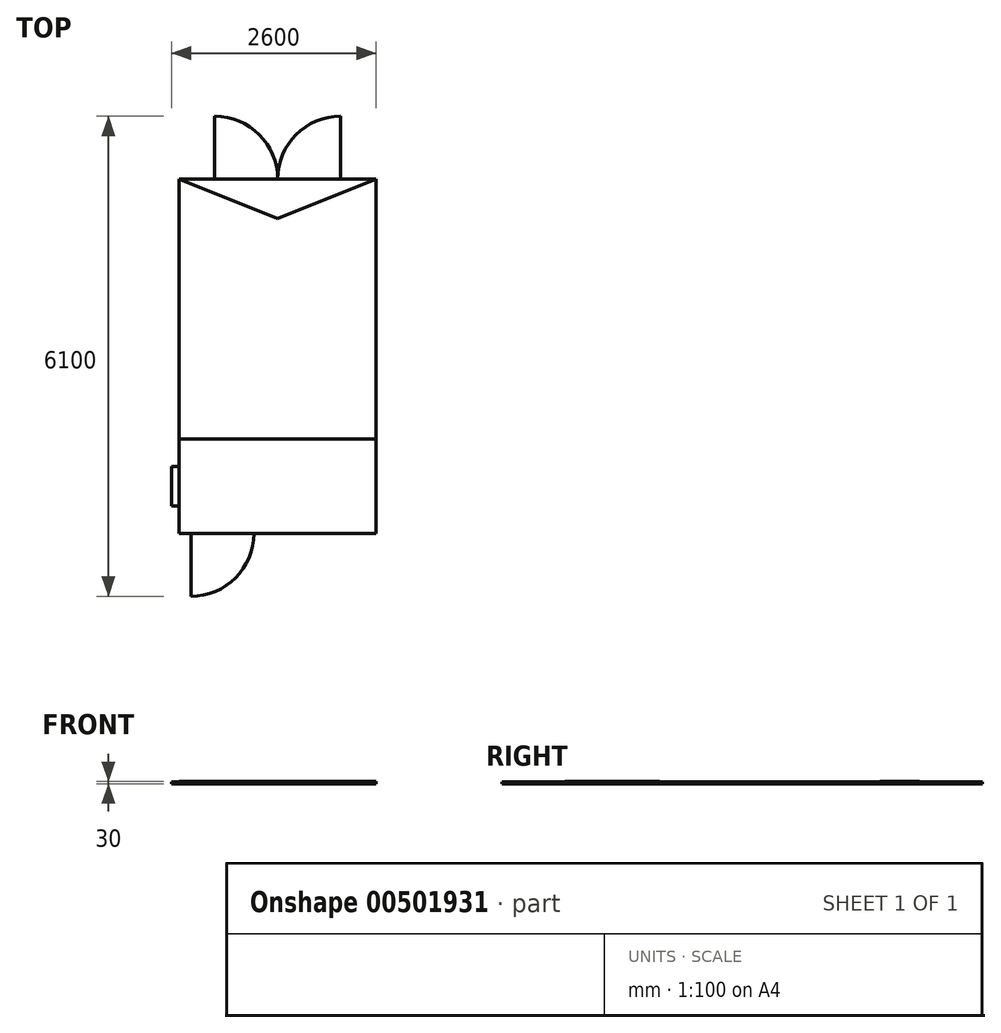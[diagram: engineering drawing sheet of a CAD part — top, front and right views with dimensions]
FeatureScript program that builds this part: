
annotation { "Feature Type Name" : "Feature", "Feature Type Description" : "" }
export const myFeature = defineFeature(function(context is Context, id is Id, definition is map)
    precondition{}
    {
        {
            var Q0;
            Q0=qCreatedBy(makeId("Top.planeOp"),FACE);
            var sketch = newSketch(context, id + "F0", { "sketchPlane" : qUnion([Q0])});
            skLineSegment(sketch, "E0.bottom", {"start": v(0, 0) * mm, "end": v(2500, 0) * mm});
            skLineSegment(sketch, "E0.top", {"start": v(0, 4500) * mm, "end": v(2500, 4500) * mm});
            skLineSegment(sketch, "E0.left", {"start": v(0, 0) * mm, "end": v(0, 4500) * mm});
            skLineSegment(sketch, "E0.right", {"start": v(2500, 0) * mm, "end": v(2500, 4500) * mm});
            skLineSegment(sketch, "E1", {"start": v(0, 1200) * mm, "end": v(2500, 1200) * mm});
            skLineSegment(sketch, "E2", {"start": v(0, 4500) * mm, "end": v(1250, 4000) * mm});
            skLineSegment(sketch, "E3", {"start": v(1250, 4000) * mm, "end": v(2500, 4500) * mm});
            skLineSegment(sketch, "E4", {"start": v(450, 4500) * mm, "end": v(450, 5300) * mm});
            skArc(sketch, "E5", {"start": v(1250, 4500) * mm, "mid": v(1015.69, 5065.69) * mm, "end": v(450, 5300) * mm});
            skLineSegment(sketch, "E6", {"start": v(2050, 4500) * mm, "end": v(2050, 5300) * mm});
            skArc(sketch, "E7", {"start": v(2050, 5300) * mm, "mid": v(1484.31, 5065.69) * mm, "end": v(1250, 4500) * mm});
            skLineSegment(sketch, "E8", {"start": v(0, 850) * mm, "end": v(-100, 850) * mm});
            skLineSegment(sketch, "E9", {"start": v(-100, 850) * mm, "end": v(-100, 350) * mm});
            skLineSegment(sketch, "E10", {"start": v(-100, 350) * mm, "end": v(0, 350) * mm});
            skLineSegment(sketch, "E11", {"start": v(147.95, 0) * mm, "end": v(147.95, -800) * mm});
            skArc(sketch, "E12", {"start": v(147.95, -800) * mm, "mid": v(713.64, -565.69) * mm, "end": v(947.95, 0) * mm});
            skSolve(sketch);
        }
        {
            var Q0;
            {var subQ0=sQuery(id+"F0.wireOp",EDGE,"E4");Q0=makeQuery(id+"F0.imprint","IMPRINT",FACE,{"disambiguationData":[TD([[makeQuery(id+"F0.imprint","IMPRINT",EDGE,{"derivedFrom":subQ0}),-1.0]])]});}
            var Q1;
            {var subQ2=sQuery(id+"F0.wireOp",EDGE,"E6");Q1=makeQuery(id+"F0.imprint","IMPRINT",FACE,{"disambiguationData":[TD([[makeQuery(id+"F0.imprint","IMPRINT",EDGE,{"derivedFrom":subQ2}),1.0]])]});}
            var Q2;
            {var subQ1=sQuery(id+"F0.wireOp",EDGE,"E1");Q2=makeQuery(id+"F0.imprint","IMPRINT",FACE,{"disambiguationData":[TD([[makeQuery(id+"F0.imprint","IMPRINT",EDGE,{"derivedFrom":subQ1}),1.0]])]});}
            var Q3;
            {var subQ0=sQuery(id+"F0.wireOp",EDGE,"E8");Q3=makeQuery(id+"F0.imprint","IMPRINT",FACE,{"disambiguationData":[TD([[makeQuery(id+"F0.imprint","IMPRINT",EDGE,{"derivedFrom":subQ0}),1.0]])]});}
            var Q4;
            {var subQ0=sQuery(id+"F0.wireOp",EDGE,"E11");Q4=makeQuery(id+"F0.imprint","IMPRINT",FACE,{"disambiguationData":[TD([[makeQuery(id+"F0.imprint","IMPRINT",EDGE,{"derivedFrom":subQ0}),1.0]])]});}
            extrude(context, id + "F1", {"entities" : qUnion([Q0, Q1, Q2, Q3, Q4]), "depth" : 25 * mm});
        }
        {
            var Q0;
            {var subQ5=sQuery(id+"F0.wireOp",EDGE,"E2");Q0=makeQuery(id+"F0.imprint","IMPRINT",FACE,{"disambiguationData":[TD([[makeQuery(id+"F0.imprint","IMPRINT",EDGE,{"derivedFrom":subQ5}),1.0]])]});}
            extrude(context, id + "F2", {"entities" : qUnion([Q0]), "operationType" : NewBodyOperationType.ADD, "depth" : 30 * mm});
        }
        {
            var Q0;
            {var subQ7=sQuery(id+"F0.wireOp",EDGE,"E1");Q0=makeQuery(id+"F0.imprint","IMPRINT",FACE,{"disambiguationData":[TD([[makeQuery(id+"F0.imprint","IMPRINT",EDGE,{"derivedFrom":subQ7}),-1.0]])]});}
            extrude(context, id + "F3", {"entities" : qUnion([Q0]), "operationType" : NewBodyOperationType.ADD, "depth" : 30 * mm});
        }
    });
